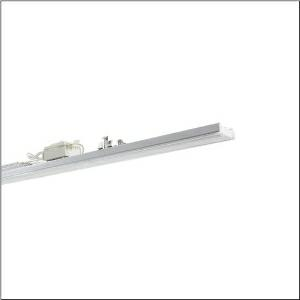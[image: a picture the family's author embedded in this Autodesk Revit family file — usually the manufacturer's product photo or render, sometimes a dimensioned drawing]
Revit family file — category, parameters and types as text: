
# Revit family: licross_r__21_recessed_mo_52tl18dv46xgd_4360
name_source: partatom
category: Lighting Fixtures
units: mm (PartAtom-declared; Revit-internal decimal feet)

## family parameters
Cut with Voids When Loaded = No
Host = Face
Light Source = No
Part Type = Normal
Room Calculation Point = No
Round Connector Dimension = Use Diameter
Shared = No

## types (1)
- --- (1 x LED, 940 lm, 4.6 W, 4000K)
    Apparent Load = 5 VA
    CIE Flux Codes = 79 95 99 100 100
    Color Rendering = 80
    Color Temperature = 4000K
    Default Elevation = 1800 mm
    Description = Licross® 21 Recessed MO, luminaire insert, of sheet steel, galvanised, coil coated, white, length: 2.250mm, width: 66mm, height: 67mm, LED rated luminous flux: 6.200lm, light colour: 840, control gear: DALI 2 (for two DALI lines), with plug, 5-pole, with phase selection, mains connection: 220..240V, AC/DC, 0/50..60Hz, rated input power: 35W, internal wiring halogen-free, for central battery installations according to DIN EN 60598-2-22, for emergency light function, without changeover relay, primary light control with lens, of plastic, primary optical cover: cover, of PMMA, light emission: direct distribution, primary light characteristic: symmetric, protection rating (complete): IP40, insulation class (complete): insulation class I (protective earthing), certification: CE, ENEC, VDE, UKCA, protection symbol: D if used in an environment without relevant dust loads with corresponding accessories, impact resistance: IK06, permissible ambient temperature for indoor applications: -25..+45°C, standard: EN 60598-2-22, corresponds to IFS (International Featured Standards) requirements for safety and quality in the food industry, reducing of maximum allowable ambient temperature of 5°C with ceiling mounting, LABS conformity tested according to VDMA 24364:2018-05, packaging unit: 1 piece
    Height = 58 mm
    Lamp = 1 x LED
    Lamp Light Flux = 940 lm
    Lamp Power = 4.6 W
    Lamp count = 1
    Length = 2250 mm
    Luminous efficacy = 204 lm/W
    Manufacturer = Siteco
    ModVariant = No
    Model = 52TL18DV46XGD
    Mounting Place = Ceiling
    Mounting Type = Pendant
    Number of Poles = 1
    OnlyDefault = Yes
    Power Factor = 1
    Product Name = Licross® 21 Recessed MO
    Product group = luminaire insert | ceiling pendant
    ProductGroupID = 902
    Protection Class = Protection class I
    Protection Degree = IP 40
    RLX_Detail_Level = 1
    RLX_Emergency_Light_Flux = 0 lm
    RLX_Emergency_Type = 0
    RLX_Emergency_Type_DB = No
    RlxData = <blob elided: 29461 chars, md5=b2fcc164>
    Socket = socket
    Standby Power = 0 W
    System Light Flux = 940 lm
    System Power = 5 W
    Type Comments = : DC mode (central or group accumulator) initial emergency light level
    Type Image = l_1296930.jpg
    URL = http://relux.com
    VarID = @adj_061749
    Voltage = 0 V
    Weight = 0.00 kg
    Width = 66 mm

## geometry (parser evidence)
native form markers: Blend x4, Sweep x10
no freeform markers — native parametric forms only
